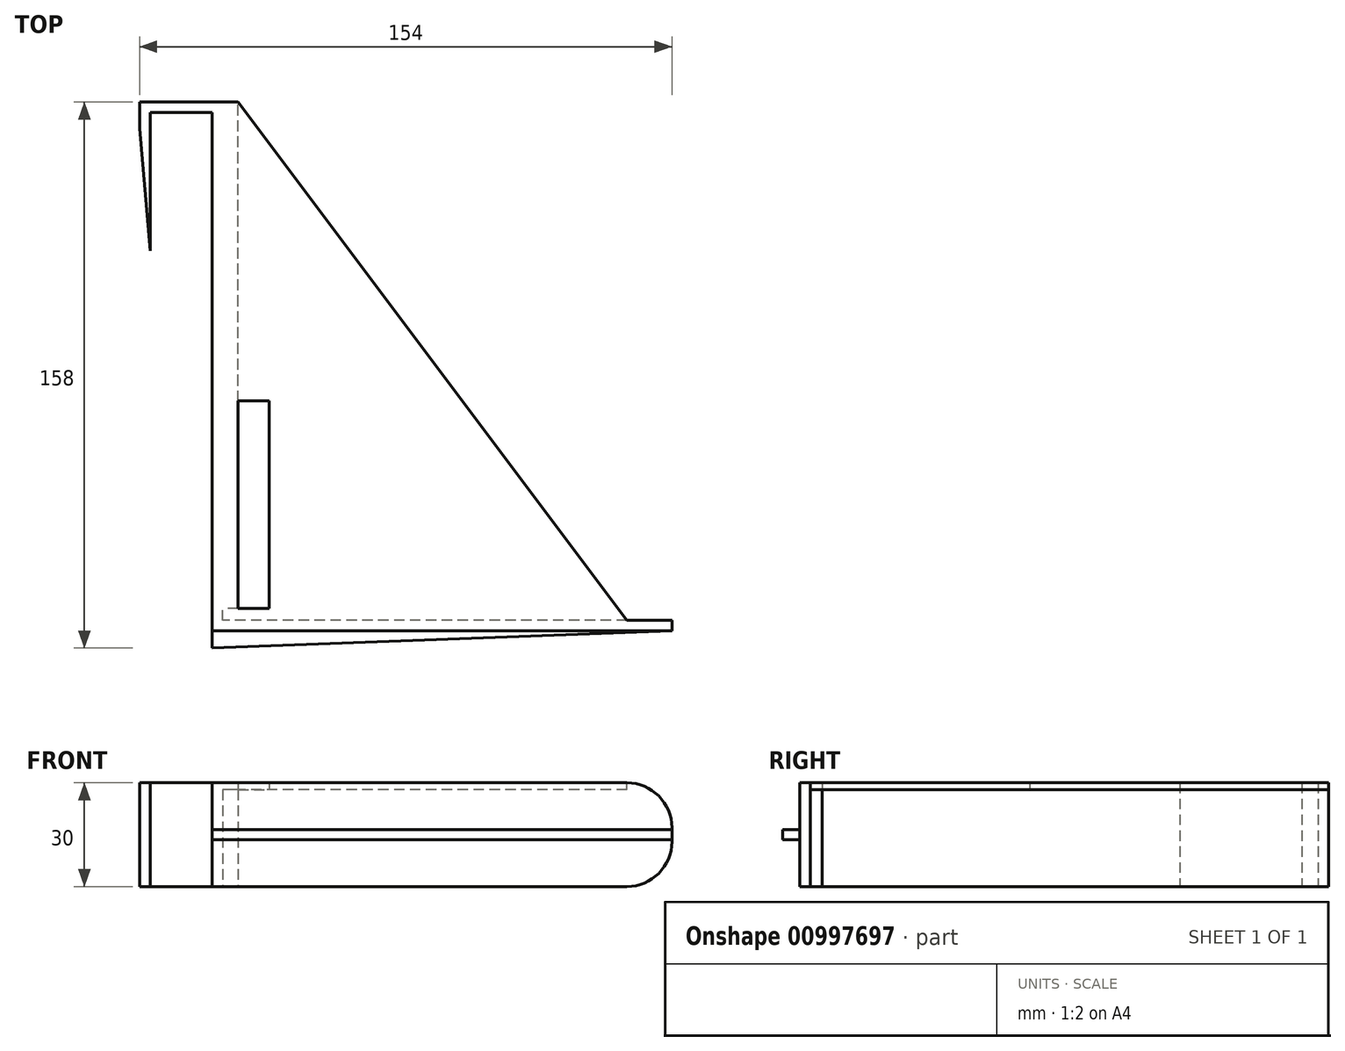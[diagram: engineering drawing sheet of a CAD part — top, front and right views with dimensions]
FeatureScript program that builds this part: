
annotation { "Feature Type Name" : "Feature", "Feature Type Description" : "" }
export const myFeature = defineFeature(function(context is Context, id is Id, definition is map)
    precondition{}
    {
        {
            var Q0;
            Q0=qCreatedBy(makeId("Top.planeOp"),FACE);
            var sketch = newSketch(context, id + "F0", { "sketchPlane" : qUnion([Q0])});
            skLineSegment(sketch, "E0", {"start": v(-48.26, -2.63) * mm, "end": v(-48.26, 37.37) * mm});
            skLineSegment(sketch, "E1", {"start": v(-48.26, 37.37) * mm, "end": v(-30.26, 37.37) * mm});
            skLineSegment(sketch, "E2", {"start": v(-30.26, 37.37) * mm, "end": v(-30.26, -112.63) * mm});
            skLineSegment(sketch, "E3", {"start": v(-30.26, -112.63) * mm, "end": v(102.74, -112.63) * mm});
            skLineSegment(sketch, "E4", {"start": v(102.74, -112.63) * mm, "end": v(102.74, -109.63) * mm});
            skLineSegment(sketch, "E5", {"start": v(102.74, -109.63) * mm, "end": v(-27.26, -109.63) * mm});
            skLineSegment(sketch, "E6", {"start": v(-27.26, -109.63) * mm, "end": v(-27.26, 40.37) * mm});
            skLineSegment(sketch, "E7", {"start": v(-27.26, 40.37) * mm, "end": v(-51.26, 40.37) * mm});
            skLineSegment(sketch, "E8", {"start": v(-51.26, 40.37) * mm, "end": v(-51.26, 32.67) * mm});
            skLineSegment(sketch, "E9", {"start": v(-51.26, 32.67) * mm, "end": v(-48.26, -2.63) * mm});
            skSolve(sketch);
        }
        {
            var Q0;
            Q0=makeQuery(id+"F0.imprint","IMPRINT",FACE,{"disambiguationData":[TD([[makeQuery(id+"F0.imprint","IMPRINT",EDGE,{"derivedFrom":sQuery(id+"F0.wireOp",EDGE,"E0")}),1.0]])]});
            extrude(context, id + "F1", {"entities" : qUnion([Q0]), "depth" : 30 * mm, "offsetDistance" : 25 * mm});
        }
        {
            var Q0;
            Q0=makeQuery(id+"F1.opExtrude","SWEPT_FACE",FACE,{"disambiguationData":[OSD([sQuery(id+"F0.wireOp",EDGE,"E3")])]});
            var sketch = newSketch(context, id + "F2", { "sketchPlane" : qUnion([Q0])});
            skLineSegment(sketch, "E10.bottom", {"start": v(102.74, 16.5) * mm, "end": v(-30.26, 16.5) * mm});
            skLineSegment(sketch, "E10.top", {"start": v(102.74, 13.5) * mm, "end": v(-30.26, 13.5) * mm});
            skLineSegment(sketch, "E10.left", {"start": v(102.74, 16.5) * mm, "end": v(102.74, 13.5) * mm});
            skLineSegment(sketch, "E10.right", {"start": v(-30.26, 16.5) * mm, "end": v(-30.26, 13.5) * mm});
            skSolve(sketch);
        }
        {
            var Q0;
            Q0=makeQuery(id+"F2.imprint","IMPRINT",FACE,{"disambiguationData":[TD([[makeQuery(id+"F2.imprint","IMPRINT",EDGE,{"derivedFrom":sQuery(id+"F2.wireOp",EDGE,"E10.bottom")}),1.0]])]});
            extrude(context, id + "F3", {"entities" : qUnion([Q0]), "operationType" : NewBodyOperationType.ADD, "depth" : 5 * mm, "offsetDistance" : 25 * mm});
        }
        {
            var Q0;
            Q0=makeQuery(id+"F3.opExtrude","SWEPT_FACE",FACE,{"disambiguationData":[OSD([sQuery(id+"F2.wireOp",EDGE,"E10.bottom")])]});
            var sketch = newSketch(context, id + "F4", { "sketchPlane" : qUnion([Q0])});
            skLineSegment(sketch, "E11", {"start": v(-30.26, -117.63) * mm, "end": v(102.74, -112.63) * mm});
            skLineSegment(sketch, "E12", {"start": v(102.74, -112.63) * mm, "end": v(102.74, -117.63) * mm});
            skLineSegment(sketch, "E13", {"start": v(102.74, -117.63) * mm, "end": v(-30.26, -117.63) * mm});
            skSolve(sketch);
        }
        {
            var Q0;
            Q0=makeQuery(id+"F4.imprint","IMPRINT",FACE,{"disambiguationData":[TD([[makeQuery(id+"F4.imprint","IMPRINT",EDGE,{"derivedFrom":sQuery(id+"F4.wireOp",EDGE,"E11")}),-1.0]])]});
            extrude(context, id + "F5", {"entities" : qUnion([Q0]), "operationType" : NewBodyOperationType.REMOVE, "endBound" : BoundingType.THROUGH_ALL, "oppositeDirection" : true, "depth" : 25 * mm, "offsetDistance" : 25 * mm});
        }
        {
            var Q0;
            Q0=makeQuery(id+"F1.opExtrude","CAP_EDGE",EDGE,{"disambiguationData":[OSD([sQuery(id+"F0.wireOp",EDGE,"E4")])],"isStart":true});
            var Q1;
            Q1=makeQuery(id+"F1.opExtrude","CAP_EDGE",EDGE,{"disambiguationData":[OSD([sQuery(id+"F0.wireOp",EDGE,"E4")])],"isStart":false});
            fillet(context, id + "F6", {"entities" : qUnion([Q0, Q1]), "radius" : 13 * mm, "tangentPropagation" : true, "allowEdgeOverflow" : false});
        }
        {
            var Q0;
            Q0=makeQuery(id+"F1.opExtrude","SWEPT_FACE",FACE,{"disambiguationData":[OSD([sQuery(id+"F0.wireOp",EDGE,"E6")])]});
            var sketch = newSketch(context, id + "F7", { "sketchPlane" : qUnion([Q0])});
            skLineSegment(sketch, "E14.bottom", {"start": v(40.37, 30) * mm, "end": v(-106.13, 30) * mm});
            skLineSegment(sketch, "E14.top", {"start": v(40.37, 0) * mm, "end": v(-106.13, 0) * mm});
            skLineSegment(sketch, "E14.left", {"start": v(40.37, 30) * mm, "end": v(40.37, 0) * mm});
            skLineSegment(sketch, "E14.right", {"start": v(-106.13, 30) * mm, "end": v(-106.13, 0) * mm});
            skSolve(sketch);
        }
        {
            var Q0;
            Q0=makeQuery(id+"F7.imprint","IMPRINT",FACE,{"disambiguationData":[TD([[makeQuery(id+"F7.imprint","IMPRINT",EDGE,{"derivedFrom":sQuery(id+"F7.wireOp",EDGE,"E14.bottom")}),-1.0]])]});
            extrude(context, id + "F8", {"entities" : qUnion([Q0]), "operationType" : NewBodyOperationType.ADD, "depth" : 4.5 * mm, "offsetDistance" : 25 * mm});
        }
        {
            var Q0;
            Q0=makeQuery(id+"F8.boolean.opBoolean","MERGE",FACE,{"derivedFrom":[makeQuery(id+"F1.opExtrude","CAP_FACE",FACE,{"disambiguationData":[OSD([sQuery(id+"F0.wireOp",EDGE,"E0"),sQuery(id+"F0.wireOp",EDGE,"E1"),sQuery(id+"F0.wireOp",EDGE,"E2"),sQuery(id+"F0.wireOp",EDGE,"E3"),sQuery(id+"F0.wireOp",EDGE,"E4"),sQuery(id+"F0.wireOp",EDGE,"E5"),sQuery(id+"F0.wireOp",EDGE,"E6"),sQuery(id+"F0.wireOp",EDGE,"E7"),sQuery(id+"F0.wireOp",EDGE,"E8"),sQuery(id+"F0.wireOp",EDGE,"E9")])],"isStart":false}),makeQuery(id+"F8.opExtrude","SWEPT_FACE",FACE,{"disambiguationData":[OSD([sQuery(id+"F7.wireOp",EDGE,"E14.bottom")])]})]});
            var sketch = newSketch(context, id + "F9", { "sketchPlane" : qUnion([Q0])});
            skLineSegment(sketch, "E15", {"start": v(-30.26, 37.37) * mm, "end": v(-30.26, -112.63) * mm});
            skLineSegment(sketch, "E16", {"start": v(-30.26, -112.63) * mm, "end": v(89.74, -112.63) * mm});
            skLineSegment(sketch, "E17", {"start": v(89.74, -112.63) * mm, "end": v(89.74, -109.63) * mm});
            skLineSegment(sketch, "E18", {"start": v(89.74, -109.63) * mm, "end": v(-22.76, 40.37) * mm});
            skLineSegment(sketch, "E19", {"start": v(-22.76, 40.37) * mm, "end": v(-30.26, 40.37) * mm});
            skLineSegment(sketch, "E20", {"start": v(-30.26, 40.37) * mm, "end": v(-30.26, 37.37) * mm});
            skSolve(sketch);
        }
        {
            var Q0;
            Q0=makeQuery(id+"F9.imprint","IMPRINT",FACE,{"disambiguationData":[TD([[makeQuery(id+"F9.imprint","IMPRINT",EDGE,{"derivedFrom":sQuery(id+"F9.wireOp",EDGE,"E18")}),1.0]])]});
            extrude(context, id + "F10", {"entities" : qUnion([Q0]), "operationType" : NewBodyOperationType.ADD, "oppositeDirection" : true, "depth" : 2 * mm, "offsetDistance" : 25 * mm});
        }
        {
            var Q0;
            Q0=makeQuery(id+"F10.opExtrude","CAP_FACE",FACE,{"disambiguationData":[OSD([sQuery(id+"F0.wireOp",EDGE,"E5"),sQuery(id+"F0.wireOp",EDGE,"E6"),sQuery(id+"F7.wireOp",EDGE,"E14.bottom"),sQuery(id+"F7.wireOp",EDGE,"E14.right"),sQuery(id+"F9.wireOp",EDGE,"E18")])],"isStart":false});
            var sketch = newSketch(context, id + "F11", { "sketchPlane" : qUnion([Q0])});
            skLineSegment(sketch, "E21.bottom", {"start": v(-22.76, 106.13) * mm, "end": v(-13.76, 106.13) * mm});
            skLineSegment(sketch, "E21.top", {"start": v(-22.76, 46.13) * mm, "end": v(-13.76, 46.13) * mm});
            skLineSegment(sketch, "E21.left", {"start": v(-22.76, 106.13) * mm, "end": v(-22.76, 46.13) * mm});
            skLineSegment(sketch, "E21.right", {"start": v(-13.76, 106.13) * mm, "end": v(-13.76, 46.13) * mm});
            skSolve(sketch);
        }
        {
            var Q0;
            Q0=makeQuery(id+"F11.imprint","IMPRINT",FACE,{"disambiguationData":[TD([[makeQuery(id+"F11.imprint","IMPRINT",EDGE,{"derivedFrom":sQuery(id+"F11.wireOp",EDGE,"E21.bottom")}),-1.0]])]});
            extrude(context, id + "F12", {"entities" : qUnion([Q0]), "operationType" : NewBodyOperationType.REMOVE, "endBound" : BoundingType.THROUGH_ALL, "oppositeDirection" : true, "depth" : 25 * mm, "offsetDistance" : 25 * mm});
        }
    });
